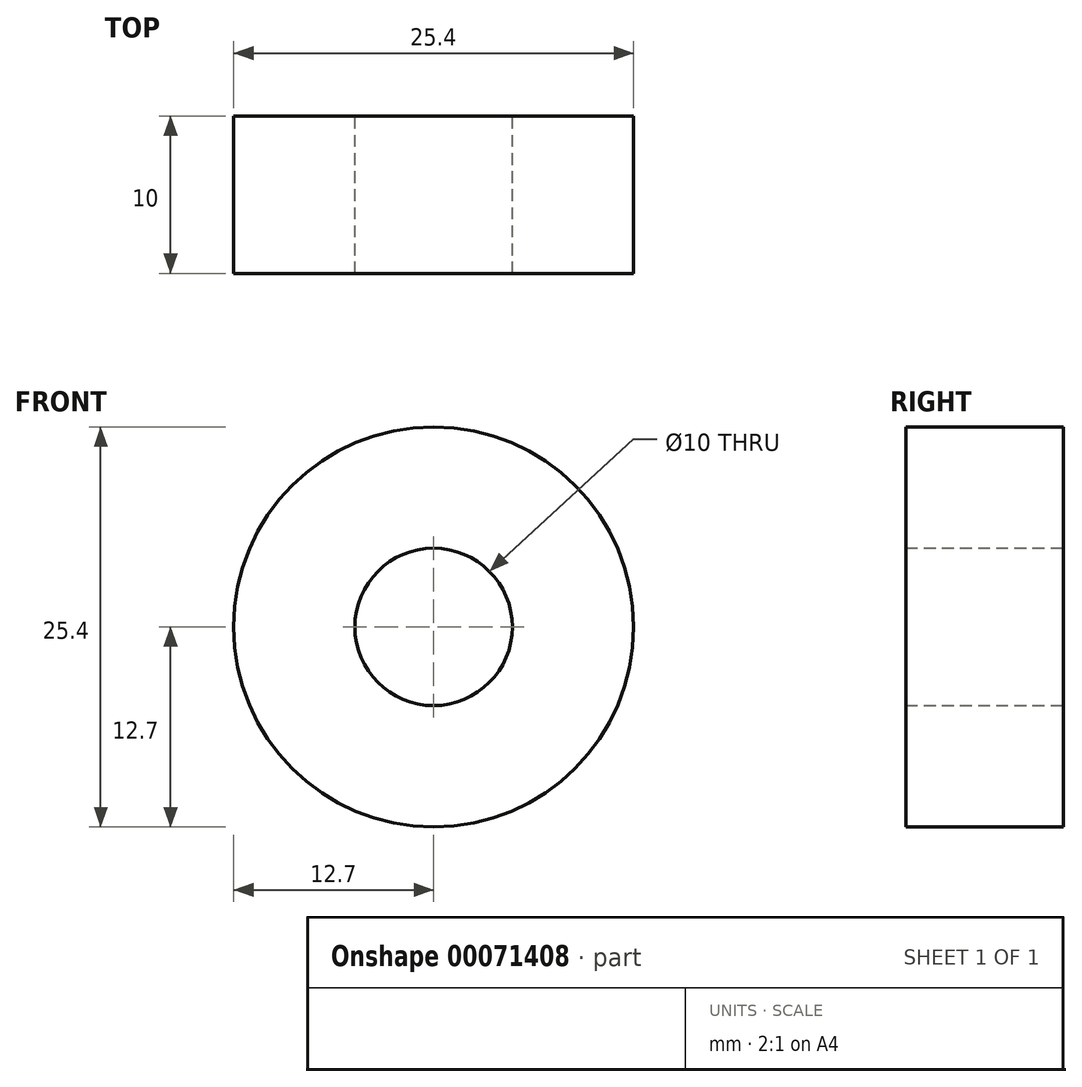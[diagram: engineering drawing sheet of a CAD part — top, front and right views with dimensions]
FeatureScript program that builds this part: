
annotation { "Feature Type Name" : "Feature", "Feature Type Description" : "" }
export const myFeature = defineFeature(function(context is Context, id is Id, definition is map)
    precondition{}
    {
        {
            var Q0;
            Q0=qCreatedBy(makeId("Front.planeOp"),FACE);
            var sketch = newSketch(context, id + "F0", { "sketchPlane" : qUnion([Q0])});
            skCircle(sketch, "E0", {"center": v(0, 0) * mm, "radius": 12.7 * mm});
            skCircle(sketch, "E1", {"center": v(0, 0) * mm, "radius": 5 * mm});
            skSolve(sketch);
        }
        {
            var Q0;
            Q0=makeQuery(id+"F0.imprint","IMPRINT",FACE,{"disambiguationData":[TD([[makeQuery(id+"F0.imprint","IMPRINT",EDGE,{"derivedFrom":sQuery(id+"F0.wireOp",EDGE,"E0")}),1.0]])]});
            extrude(context, id + "F1", {"entities" : qUnion([Q0]), "depth" : 10 * mm});
        }
    });
